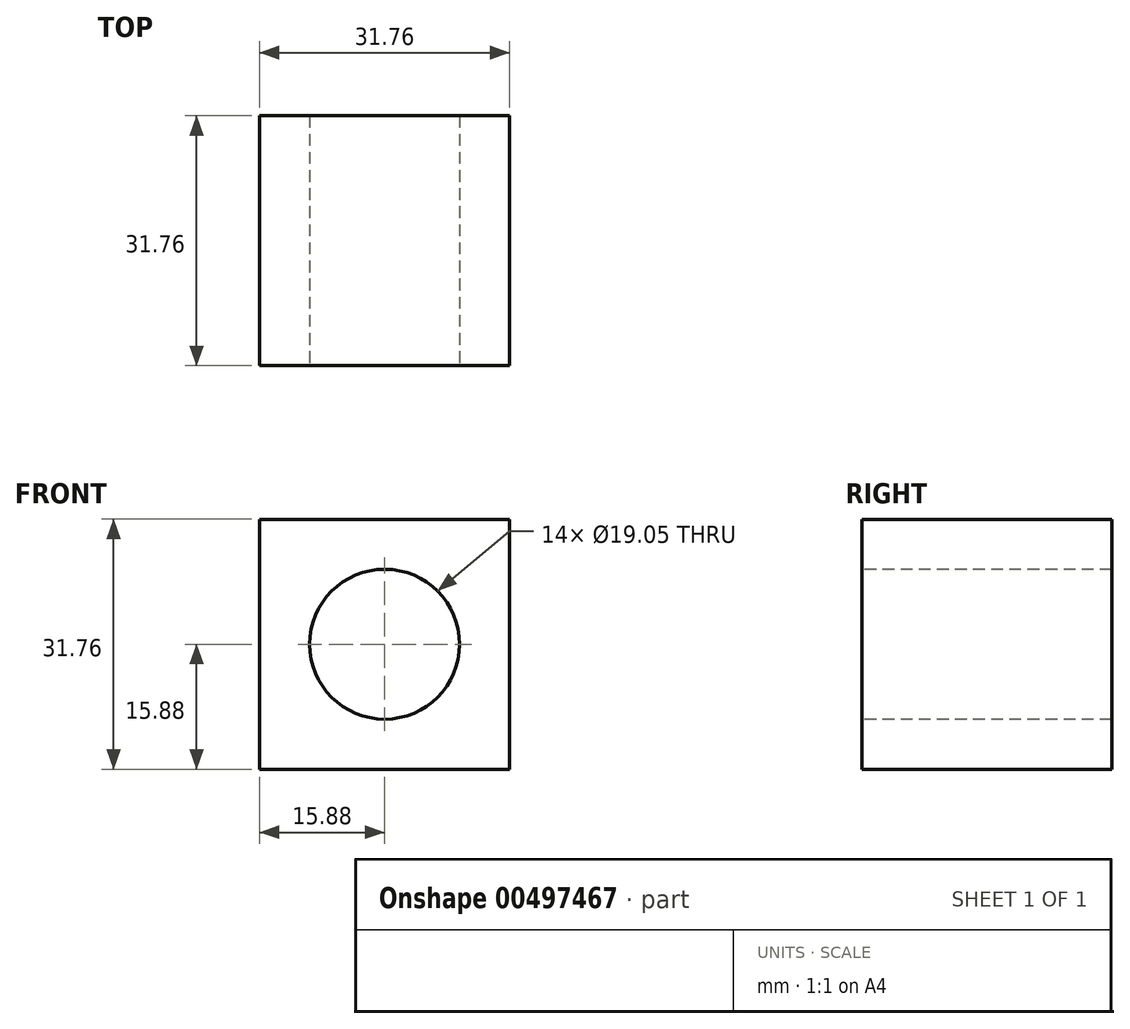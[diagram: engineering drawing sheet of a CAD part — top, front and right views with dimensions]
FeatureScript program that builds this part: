
annotation { "Feature Type Name" : "Feature", "Feature Type Description" : "" }
export const myFeature = defineFeature(function(context is Context, id is Id, definition is map)
    precondition{}
    {
        {
            var Q0;
            Q0=qCreatedBy(makeId("Front.planeOp"),FACE);
            var sketch = newSketch(context, id + "F0", { "sketchPlane" : qUnion([Q0])});
            skLineSegment(sketch, "E0.bottom", {"start": v(15.87, 15.88) * mm, "end": v(-15.88, 15.88) * mm});
            skLineSegment(sketch, "E0.top", {"start": v(15.88, -15.88) * mm, "end": v(-15.87, -15.88) * mm});
            skLineSegment(sketch, "E0.left", {"start": v(15.87, 15.88) * mm, "end": v(15.88, -15.88) * mm});
            skLineSegment(sketch, "E0.right", {"start": v(-15.88, 15.88) * mm, "end": v(-15.87, -15.88) * mm});
            skPoint(sketch, "E0.middle", {"position": v(0, 0) * mm});
            skSolve(sketch);
        }
        {
            var Q0;
            Q0=makeQuery(id+"F0.imprint","IMPRINT",FACE,{"disambiguationData":[TD([[makeQuery(id+"F0.imprint","IMPRINT",EDGE,{"derivedFrom":sQuery(id+"F0.wireOp",EDGE,"E0.bottom")}),1.0]])]});
            extrude(context, id + "F1", {"entities" : qUnion([Q0]), "endBound" : BoundingType.SYMMETRIC, "depth" : 31.75 * mm});
        }
        {
            var Q0;
            Q0=makeQuery(id+"F1.opExtrude","CAP_FACE",FACE,{"disambiguationData":[OSD([sQuery(id+"F0.wireOp",EDGE,"E0.bottom"),sQuery(id+"F0.wireOp",EDGE,"E0.top"),sQuery(id+"F0.wireOp",EDGE,"E0.left"),sQuery(id+"F0.wireOp",EDGE,"E0.right")])],"isStart":false});
            var sketch = newSketch(context, id + "F2", { "sketchPlane" : qUnion([Q0])});
            skCircle(sketch, "E1", {"center": v(0, 0) * mm, "radius": 9.53 * mm});
            skSolve(sketch);
        }
        {
            var Q0;
            Q0=sQuery(id+"F2.wireOp",VERTEX,"E1.center");
            var Q1;
            Q1=makeQuery(id+"F1.opExtrude","SWEPT_BODY",BODY,{"disambiguationData":[OSD([sQuery(id+"F0.wireOp",EDGE,"E0.bottom"),sQuery(id+"F0.wireOp",EDGE,"E0.top"),sQuery(id+"F0.wireOp",EDGE,"E0.left"),sQuery(id+"F0.wireOp",EDGE,"E0.right")])]});
            hole(context, id + "F3", {"style" : HoleStyle.SIMPLE, "endStyle" : HoleEndStyle.THROUGH, "holeDiameter" : 19.05 * mm, "isTappedThrough" : true, "tappedDepth" : 12.7 * mm, "tapClearance" : 3, "locations" : qUnion([Q0]), "scope" : qUnion([Q1])});
        }
    });
